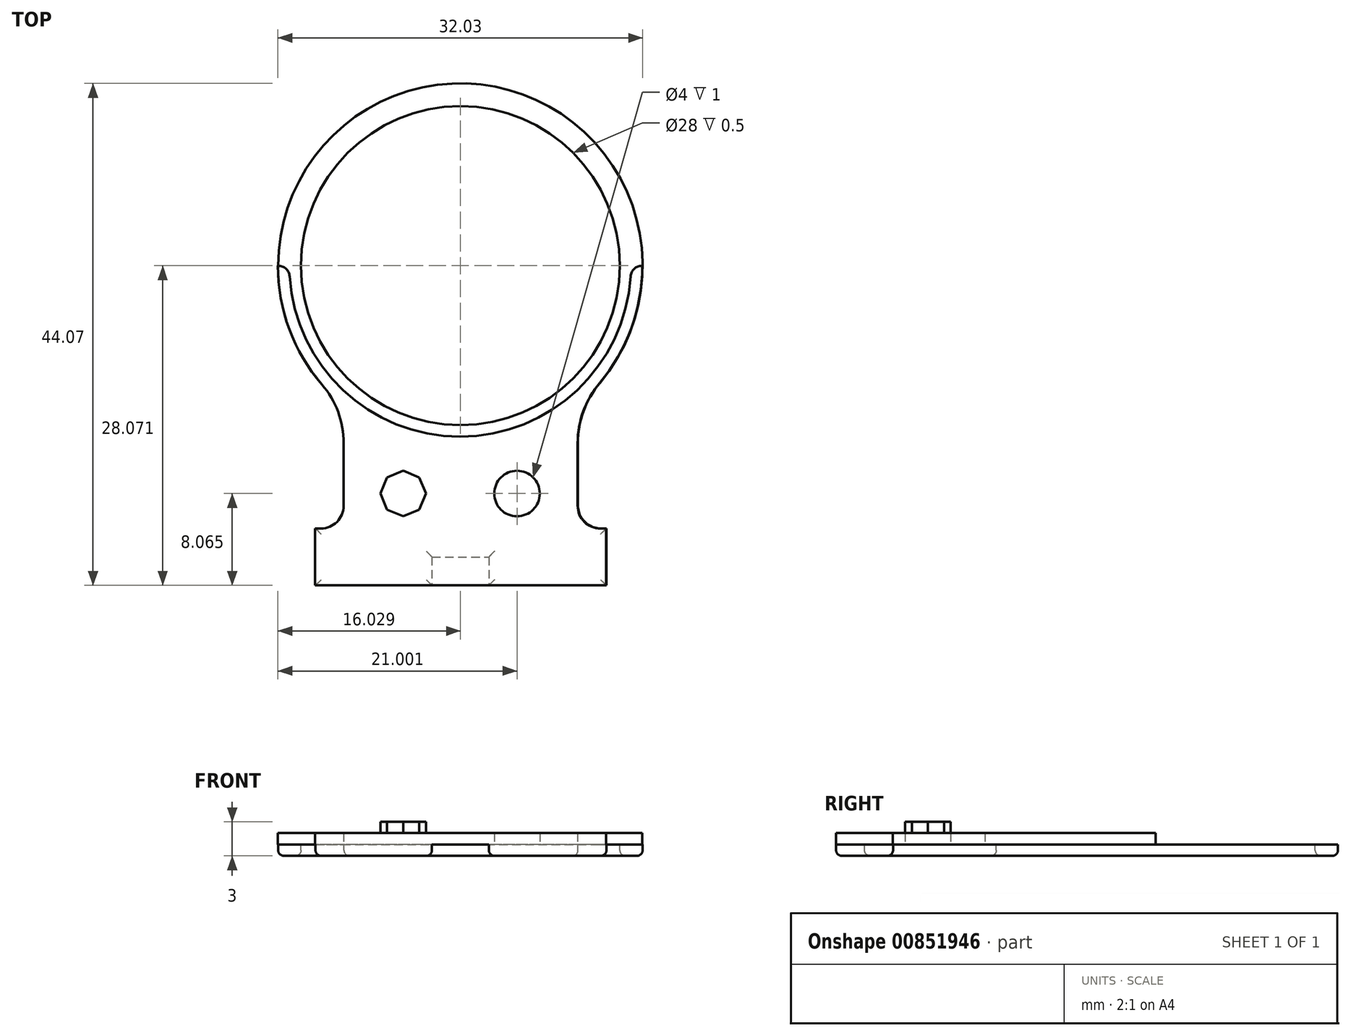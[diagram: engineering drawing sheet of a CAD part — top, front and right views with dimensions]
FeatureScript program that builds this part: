
annotation { "Feature Type Name" : "Feature", "Feature Type Description" : "" }
export const myFeature = defineFeature(function(context is Context, id is Id, definition is map)
    precondition{}
    {
        {
            var Q0;
            Q0=qCreatedBy(makeId("Top.planeOp"),FACE);
            cPlane(context, id + "F0", {"entities" : qUnion([Q0]), "cplaneType" : CPlaneType.OFFSET, "offset" : 0 * mm, "oppositeDirection" : true, "width" : 150 * mm, "height" : 150 * mm});
        }
        {
            var Q0;
            Q0=qCreatedBy(makeId("Top.planeOp"),FACE);
            cPlane(context, id + "F1", {"entities" : qUnion([Q0]), "cplaneType" : CPlaneType.OFFSET, "offset" : 0 * mm, "oppositeDirection" : true, "width" : 150 * mm, "height" : 150 * mm});
        }
        {
            var Q0;
            Q0=qCreatedBy(makeId("Top.planeOp"),FACE);
            var sketch = newSketch(context, id + "F2", { "sketchPlane" : qUnion([Q0])});
            skCircle(sketch, "E0", {"center": v(-0.2, -0.1) * mm, "radius": 15 * mm});
            skCircle(sketch, "E1", {"center": v(-0.2, -0.1) * mm, "radius": 16 * mm});
            skCircle(sketch, "E2", {"center": v(-0.2, -0.1) * mm, "radius": 14 * mm});
            skLineSegment(sketch, "E3", {"start": v(2.3, -25.67) * mm, "end": v(2.3, -28.17) * mm});
            skLineSegment(sketch, "E4", {"start": v(-2.7, -25.67) * mm, "end": v(-2.7, -28.17) * mm});
            skLineSegment(sketch, "E5", {"start": v(-15.2, -0.1) * mm, "end": v(-16.2, -0.1) * mm});
            skLineSegment(sketch, "E6", {"start": v(14.8, -0.1) * mm, "end": v(15.8, -0.1) * mm});
            skArc(sketch, "E7", {"start": v(10.12, -15.67) * mm, "mid": v(10.62, -12.86) * mm, "end": v(12.04, -10.4) * mm});
            skArc(sketch, "E8", {"start": v(-10.43, -15.67) * mm, "mid": v(-10.92, -12.93) * mm, "end": v(-12.33, -10.53) * mm});
            skLineSegment(sketch, "E9", {"start": v(12.62, -23.17) * mm, "end": v(12.62, -28.17) * mm});
            skLineSegment(sketch, "E10", {"start": v(-12.93, -23.17) * mm, "end": v(-12.93, -28.17) * mm});
            skLineSegment(sketch, "E11", {"start": v(-12.93, -28.17) * mm, "end": v(-2.7, -28.17) * mm});
            skLineSegment(sketch, "E12", {"start": v(2.3, -28.17) * mm, "end": v(12.62, -28.17) * mm});
            skLineSegment(sketch, "E13", {"start": v(10.12, -15.67) * mm, "end": v(10.12, -21.17) * mm});
            skLineSegment(sketch, "E14", {"start": v(-10.43, -15.67) * mm, "end": v(-10.43, -21.17) * mm});
            skLineSegment(sketch, "E15", {"start": v(12.62, -23.17) * mm, "end": v(12.12, -23.17) * mm});
            skLineSegment(sketch, "E16", {"start": v(-12.93, -23.17) * mm, "end": v(-12.43, -23.17) * mm});
            skPoint(sketch, "E17.visualSharp", {"position": v(10.12, -23.17) * mm});
            skArc(sketch, "E17.filletArc", {"start": v(10.12, -21.17) * mm, "mid": v(10.7, -22.58) * mm, "end": v(12.12, -23.17) * mm});
            skPoint(sketch, "E18.visualSharp", {"position": v(-10.43, -23.17) * mm});
            skArc(sketch, "E18.filletArc", {"start": v(-12.43, -23.17) * mm, "mid": v(-11.01, -22.58) * mm, "end": v(-10.43, -21.17) * mm});
            skLineSegment(sketch, "E19", {"start": v(-2.7, -25.67) * mm, "end": v(2.3, -25.67) * mm});
            skSolve(sketch);
        }
        {
            var Q0;
            Q0=qCreatedBy(id+"F0.planeOp",FACE);
            var sketch = newSketch(context, id + "F3", { "sketchPlane" : qUnion([Q0])});
            skCircle(sketch, "E20", {"center": v(-0.23, -0.1) * mm, "radius": 15 * mm});
            skCircle(sketch, "E21", {"center": v(-0.23, -0.1) * mm, "radius": 16 * mm});
            skCircle(sketch, "E22", {"center": v(-0.23, -0.1) * mm, "radius": 14 * mm});
            skLineSegment(sketch, "E23", {"start": v(2.27, -25.67) * mm, "end": v(2.27, -28.17) * mm});
            skLineSegment(sketch, "E24", {"start": v(-2.73, -25.67) * mm, "end": v(-2.73, -28.17) * mm});
            skCircle(sketch, "E25", {"center": v(4.77, -20.1) * mm, "radius": 2 * mm});
            skLineSegment(sketch, "E26", {"start": v(-15.23, -0.1) * mm, "end": v(-16.23, -0.1) * mm});
            skLineSegment(sketch, "E27", {"start": v(14.77, -0.1) * mm, "end": v(15.77, -0.1) * mm});
            skArc(sketch, "E28", {"start": v(10.1, -15.67) * mm, "mid": v(10.6, -12.87) * mm, "end": v(12.02, -10.4) * mm});
            skArc(sketch, "E29", {"start": v(-10.46, -15.67) * mm, "mid": v(-10.95, -12.93) * mm, "end": v(-12.36, -10.54) * mm});
            skLineSegment(sketch, "E30.0", {"start": v(-5.23, -18.1) * mm, "end": v(-3.81, -18.7) * mm});
            skLineSegment(sketch, "E30.1", {"start": v(-3.81, -18.7) * mm, "end": v(-3.23, -20.1) * mm});
            skLineSegment(sketch, "E30.2", {"start": v(-3.23, -20.1) * mm, "end": v(-3.81, -21.52) * mm});
            skLineSegment(sketch, "E30.3", {"start": v(-3.81, -21.52) * mm, "end": v(-5.23, -22.1) * mm});
            skLineSegment(sketch, "E30.4", {"start": v(-5.23, -22.1) * mm, "end": v(-6.64, -21.52) * mm});
            skLineSegment(sketch, "E30.5", {"start": v(-6.64, -21.52) * mm, "end": v(-7.23, -20.1) * mm});
            skLineSegment(sketch, "E30.6", {"start": v(-7.23, -20.1) * mm, "end": v(-6.64, -18.7) * mm});
            skLineSegment(sketch, "E30.7", {"start": v(-6.64, -18.7) * mm, "end": v(-5.23, -18.1) * mm});
            skLineSegment(sketch, "E31", {"start": v(12.6, -23.17) * mm, "end": v(12.6, -28.17) * mm});
            skLineSegment(sketch, "E32", {"start": v(-12.96, -23.17) * mm, "end": v(-12.96, -28.17) * mm});
            skLineSegment(sketch, "E33", {"start": v(-12.96, -28.17) * mm, "end": v(-2.73, -28.17) * mm});
            skLineSegment(sketch, "E34", {"start": v(-2.73, -28.17) * mm, "end": v(2.27, -28.17) * mm});
            skLineSegment(sketch, "E35", {"start": v(2.27, -28.17) * mm, "end": v(12.6, -28.17) * mm});
            skLineSegment(sketch, "E36", {"start": v(10.1, -15.67) * mm, "end": v(10.1, -21.17) * mm});
            skLineSegment(sketch, "E37", {"start": v(-10.46, -15.67) * mm, "end": v(-10.46, -21.17) * mm});
            skLineSegment(sketch, "E38", {"start": v(12.6, -23.17) * mm, "end": v(12.1, -23.17) * mm});
            skLineSegment(sketch, "E39", {"start": v(-12.96, -23.17) * mm, "end": v(-12.46, -23.17) * mm});
            skArc(sketch, "E40.filletArc", {"start": v(10.1, -21.17) * mm, "mid": v(10.68, -22.59) * mm, "end": v(12.1, -23.17) * mm});
            skArc(sketch, "E41.filletArc", {"start": v(-12.46, -23.17) * mm, "mid": v(-11.04, -22.59) * mm, "end": v(-10.46, -21.17) * mm});
            skLineSegment(sketch, "E42", {"start": v(-2.73, -25.67) * mm, "end": v(2.27, -25.67) * mm});
            skSolve(sketch);
        }
        {
            var Q0;
            Q0=qCreatedBy(id+"F1.planeOp",FACE);
            var sketch = newSketch(context, id + "F4", { "sketchPlane" : qUnion([Q0])});
            skLineSegment(sketch, "E43.0", {"start": v(-5.22, -18.1) * mm, "end": v(-3.81, -18.7) * mm});
            skLineSegment(sketch, "E43.1", {"start": v(-3.81, -18.7) * mm, "end": v(-3.22, -20.1) * mm});
            skLineSegment(sketch, "E43.2", {"start": v(-3.22, -20.1) * mm, "end": v(-3.81, -21.52) * mm});
            skLineSegment(sketch, "E43.3", {"start": v(-3.81, -21.52) * mm, "end": v(-5.22, -22.1) * mm});
            skLineSegment(sketch, "E43.4", {"start": v(-5.22, -22.1) * mm, "end": v(-6.64, -21.52) * mm});
            skLineSegment(sketch, "E43.5", {"start": v(-6.64, -21.52) * mm, "end": v(-7.22, -20.1) * mm});
            skLineSegment(sketch, "E43.6", {"start": v(-7.22, -20.1) * mm, "end": v(-6.64, -18.7) * mm});
            skLineSegment(sketch, "E43.7", {"start": v(-6.64, -18.7) * mm, "end": v(-5.22, -18.1) * mm});
            skSolve(sketch);
        }
        {
            var Q0;
            Q0=makeQuery(id+"F3.imprint","IMPRINT",FACE,{"disambiguationData":[TD([[makeQuery(id+"F3.imprint","IMPRINT",EDGE,{"derivedFrom":sQuery(id+"F3.wireOp",EDGE,"E23")}),-1.0]])]});
            var Q1;
            {var subQ4=sQuery(id+"F3.wireOp",EDGE,"E26");Q1=makeQuery(id+"F3.imprint","IMPRINT",FACE,{"disambiguationData":[TD([[makeQuery(id+"F3.imprint","IMPRINT",EDGE,{"derivedFrom":subQ4}),1.0]])]});}
            var Q2;
            Q2=makeQuery(id+"F3.imprint","IMPRINT",FACE,{"disambiguationData":[TD([[makeQuery(id+"F3.imprint","IMPRINT",EDGE,{"derivedFrom":sQuery(id+"F3.wireOp",EDGE,"E23")}),1.0]])]});
            extrude(context, id + "F5", {"entities" : qUnion([Q0, Q1, Q2]), "depth" : 1 * mm, "offsetDistance" : 25 * mm});
        }
        {
            var Q0;
            Q0 = qSketchRegion(id + "F2", true);
            var Q1;
            Q1=makeQuery(id+"F2.imprint","IMPRINT",FACE,{"disambiguationData":[TD([[makeQuery(id+"F2.imprint","IMPRINT",EDGE,{"derivedFrom":sQuery(id+"F2.wireOp",EDGE,"E2")}),-1.0]])]});
            extrude(context, id + "F6", {"entities" : qUnion([Q0, Q1]), "operationType" : NewBodyOperationType.ADD, "oppositeDirection" : true, "depth" : 1 * mm, "offsetDistance" : 25 * mm});
        }
        {
            var Q0;
            Q0 = qSketchRegion(id + "F4", true);
            extrude(context, id + "F7", {"entities" : qUnion([Q0]), "operationType" : NewBodyOperationType.ADD, "depth" : 2 * mm, "offsetDistance" : 25 * mm});
        }
        {
            var Q0;
            Q0=makeQuery(id+"F5.opExtrude","SWEPT_EDGE",EDGE,{"disambiguationData":[OSD([sQuery(id+"F3.wireOp",EDGE,"E20"),sQuery(id+"F3.wireOp",EDGE,"E26")])]});
            var Q1;
            Q1=makeQuery(id+"F5.opExtrude","SWEPT_EDGE",EDGE,{"disambiguationData":[OSD([sQuery(id+"F3.wireOp",EDGE,"E20"),sQuery(id+"F3.wireOp",EDGE,"E27")])]});
            fillet(context, id + "F8", {"entities" : qUnion([Q0, Q1]), "radius" : 1 * mm, "tangentPropagation" : true, "allowEdgeOverflow" : false});
        }
        {
            var Q0;
            Q0=makeQuery(id+"F6.opExtrude","CAP_FACE",FACE,{"disambiguationData":[OSD([sQuery(id+"F2.wireOp",EDGE,"E1"),sQuery(id+"F2.wireOp",EDGE,"E2"),sQuery(id+"F2.wireOp",EDGE,"E3"),sQuery(id+"F2.wireOp",EDGE,"E4"),sQuery(id+"F2.wireOp",EDGE,"E7"),sQuery(id+"F2.wireOp",EDGE,"E8"),sQuery(id+"F2.wireOp",EDGE,"E9"),sQuery(id+"F2.wireOp",EDGE,"E10"),sQuery(id+"F2.wireOp",EDGE,"E11"),sQuery(id+"F2.wireOp",EDGE,"E12"),sQuery(id+"F2.wireOp",EDGE,"E13"),sQuery(id+"F2.wireOp",EDGE,"E14"),sQuery(id+"F2.wireOp",EDGE,"E15"),sQuery(id+"F2.wireOp",EDGE,"E16"),sQuery(id+"F2.wireOp",EDGE,"E17.filletArc"),sQuery(id+"F2.wireOp",EDGE,"E18.filletArc"),sQuery(id+"F2.wireOp",EDGE,"E19")])],"isStart":false});
            fillet(context, id + "F9", {"entities" : qUnion([Q0]), "radius" : .5 * mm, "tangentPropagation" : true, "allowEdgeOverflow" : false});
        }
    });
